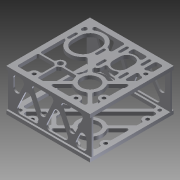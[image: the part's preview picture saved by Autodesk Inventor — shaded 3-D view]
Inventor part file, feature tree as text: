
AUTODESK INVENTOR PART (.ipt)
format: ipt  version: 2012 (Build 160160000, 160)  size: 919,552 bytes
history: native  units: in
note: dims shown in document units (in); Inventor stores cm internally (conversion verified against a paired STEP export)
features: thread x8, extrude x7, sketch x5, fillet x4, projected_geometry x1
ambient origin geometry x8: Origin, YZ Plane, XZ Plane, XY Plane, X Axis, Y Axis, Z Axis, Center Point
bodies: Solid1 (feature_tree)
feature tree (25):
  extrude  "Extrusion1"  Depth=0.1875in
  sketch  "Sketch2"  dims[d4=0.25in d5=0.25in d6=6.0in d7=0.0in]
  extrude  "Extrusion2"  Depth=6.0in TaperAngle=0.0deg
  extrude  "Extrusion3"  Depth=1.25in
  extrude  "Extrusion4"  Depth=0.375in
  fillet  "Fillet2"  Radius=0.875in
  sketch  "Sketch6"  dims[d21=0.125in d22=0.25in d24=0.25in d25=0.125in d27=0.125in d32=0.25in d33=0.0in d35=0.375in d36=0.375in d37=0.375in d38=0.375in d39=0.1719in d40=0.3438in d41=0.3438in d42=0.3438in d43=0.3438in d44=0.125in d46=0.125in d49=0.125in d50=0.125in d51=0.125in d52=0.125in d53=0.125in d54=0.125in d55=0.125in d56=0.125in d57=0.25in d58=0.0in d60=0.3798in d61=0.287in d62=0.287in d63=0.287in d64=0.125in d65=0.125in d66=0.125in d67=0.125in d68=0.125in d69=0.125in d70=0.125in d71=0.125in d72=0.125in d73=0.125in d74=0.375in d76=0.25in d77=0.375in d78=0.375in d79=0.25in d80=0.0in d81=0.25in d88=0.125in d89=1.25in d90=1.5in d91=0.75in d92=0.5in d94=0.2in d96=0.9in d97=1.0in d98=0.5in d99=0.5in d101=2.0in d102=0.2in d103=0.8in d104=0.8in d105=0.7874in d107=1.6in d108=0.7874in d110=1.6in d114=1.0in d115=1.0in d116=1.5in d117=1.0in d119=0.2in d122=4.5in d123=1.3125in d124=0.366in d126=2.3in d127=0.25in d128=0.0in d129=0.375in d131=4.5in d132=0.125in d153=0.25in d154=0.125in d156=0.375in d157=0.375in d160=0.25in d161=0.125in d162=0.25in d163=0.125in d165=0.875in d166=0.125in d168=0.3125in d169=0.125in d170=0.125in d171=1.0in d177=0.125in d178=0.6in d179=0.25in d180=0.0in d181=0.125in d183=0.25in d185=0.25in d186=0.125in d188=1.5625in d190=1.3125in d191=0.366in d193=0.25in d194=0.125in d197=1.0in d198=1.176in d199=0.1in d200=0.0in d201=0.0625in d203=0.25in d207=2.1875in d208=1.9688in d211=0.125in d212=0.3in d213=0.5in d214=0.25in d215=0.3125in d220=0.5in d221=1.5in d222=0.25in d224=0.125in d225=2.3in d226=0.35in d227=0.25in d228=1.5in d229=1.5in d230=0.5821in d231=0.25in d232=1.5in d233=0.125in d235=2.0in d236=0.25in d237=1.5in d238=0.3125in d239=0.7874in d241=3.0in d242=0.3937in d244=1.0in d246=1.5in d247=0.7874in d249=3.0in d250=0.3937in d252=1.0in d254=0.5in d255=0.25in d256=0.3125in d257=0.25in d258=0.5in d259=0.3125in d260=0.25in d262=0.625in d264=6.0in d267=0.25in d269=3.0in d270=6.0in d272=0.25in d273=0.125in d274=0.125in d275=0.1435in d276=2.0in d277=1.0in d278=0.0in d279=1.0in d280=0.0in d281=1.0in d282=0.0in d283=1.0in d284=0.0in d285=1.0in d286=0.0in d287=1.0in d288=0.0in d289=1.0in d290=0.0in d291=1.0in d292=0.0in d293=0.125in d294=0.125in d296=0.625in d297=0.25in d298=0.0625in d299=0.125in d301=1.3125in d302=0.25in d303=0.125in]
  fillet  "Fillet3"  Radius=0.25in
  extrude  "Extrusion5"  Depth=0.25in
  extrude  "Extrusion6"  Depth=0.25in
  fillet  "Fillet4"  Radius=0.125in
  extrude  "Extrusion7"  Depth=0.125in
  thread  "Thread1"  [1 undecoded]
  thread  "Thread2"  [1 undecoded]
  thread  "Thread3"  [1 undecoded]
  thread  "Thread4"  [1 undecoded]
  thread  "Thread5"  [1 undecoded]
  thread  "Thread6"  [1 undecoded]
  thread  "Thread7"  [1 undecoded]
  thread  "Thread8"  [1 undecoded]
  fillet  "Fillet5"  Radius=0.3438in
  sketch  "Sketch1"  dims[d1=3.0in d2=0.1875in d3=0.25in]
  sketch  "Sketch4"  dims[d11=1.9688in d13=1.25in]
  sketch  "Sketch5"  dims[d15=2.625in d16=1.5in d18=0.375in d19=0.875in d20=0.25in]
  projected_geometry  "Projected Loop1"
note: 8 required parameter values undecoded (feature->parameter linkage not recoverable at this tier; creation-order binding heuristic only, values carry confidence <= 0.55)
